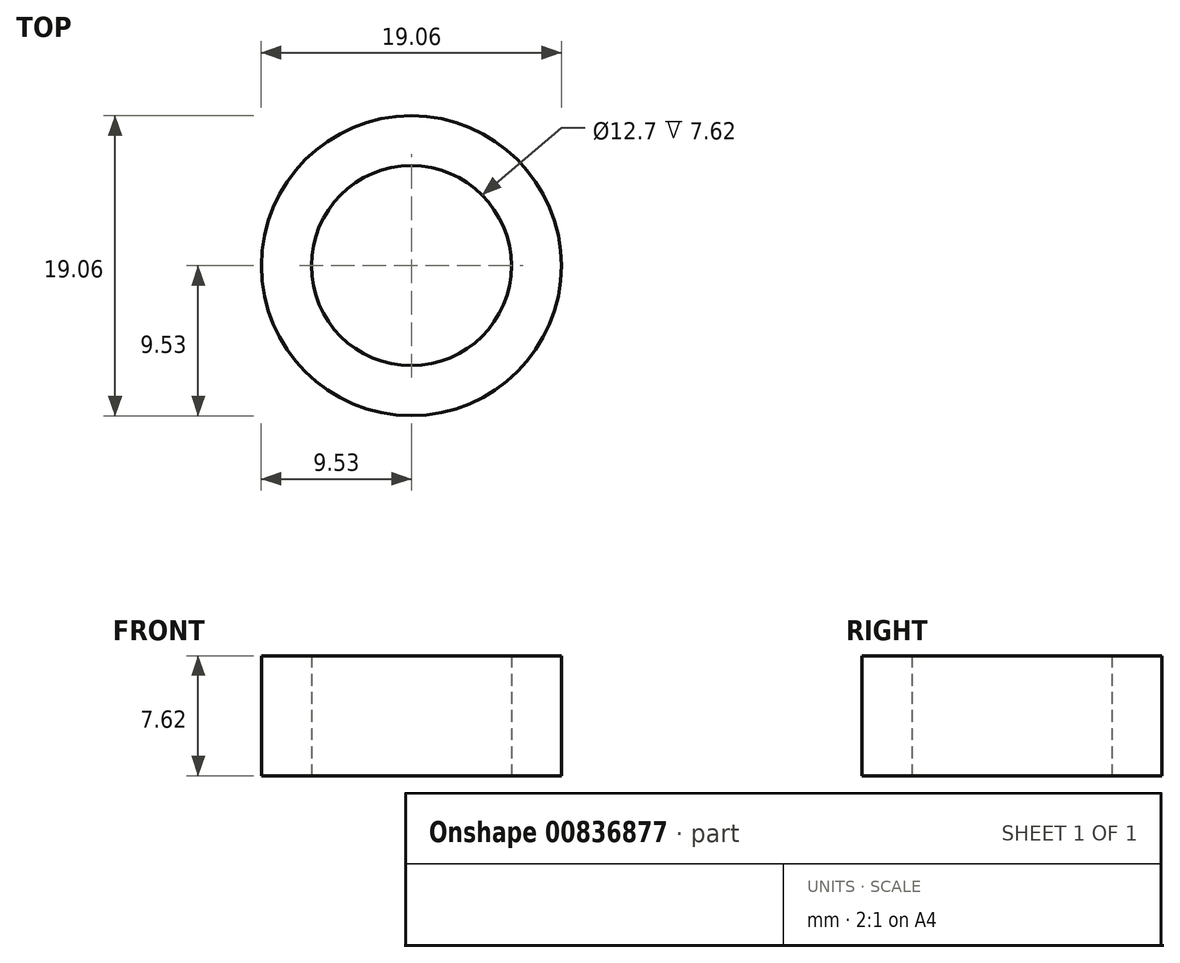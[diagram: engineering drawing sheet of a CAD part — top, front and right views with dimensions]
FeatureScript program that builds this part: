
annotation { "Feature Type Name" : "Feature", "Feature Type Description" : "" }
export const myFeature = defineFeature(function(context is Context, id is Id, definition is map)
    precondition{}
    {
        {
            var Q0;
            Q0=qCreatedBy(makeId("Top.planeOp"),FACE);
            var sketch = newSketch(context, id + "F0", { "sketchPlane" : qUnion([Q0])});
            skCircle(sketch, "E0", {"center": v(0, 0) * mm, "radius": 9.53 * mm});
            skCircle(sketch, "E1", {"center": v(0, 0) * mm, "radius": 6.35 * mm});
            skSolve(sketch);
        }
        {
            var Q0;
            Q0=makeQuery(id+"F0.imprint","IMPRINT",FACE,{"disambiguationData":[TD([[makeQuery(id+"F0.imprint","IMPRINT",EDGE,{"derivedFrom":sQuery(id+"F0.wireOp",EDGE,"E0")}),1.0]])]});
            extrude(context, id + "F1", {"entities" : qUnion([Q0]), "depth" : 7.62 * mm, "offsetDistance" : 25.4 * mm});
        }
    });
